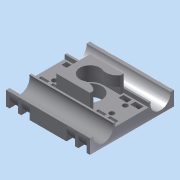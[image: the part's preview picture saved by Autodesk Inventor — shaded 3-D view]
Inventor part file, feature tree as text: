
AUTODESK INVENTOR PART (.ipt)
format: ipt  version: 2015 (Build 190159000, 159)  size: 379,392 bytes
history: native  units: in
note: dims shown in document units (in); Inventor stores cm internally (conversion verified against a paired STEP export)
features: sketch x15, extrude x10, hole x3, projected_geometry x3, move_body x3, pattern_linear x2, direct_edit x2, revolve x1
ambient origin geometry x8: Origin, YZ Plane, XZ Plane, XY Plane, X Axis, Y Axis, Z Axis, Center Point
bodies: Solid1 (feature_tree)
feature tree (39):
  sketch  "Sketch1"  dims[d0=0.7874in d1=0.7874in]
  extrude  "Extrusion1"  Depth=0.7874in
  hole  "Hole1"  [1 undecoded]
  extrude  "Extrusion2"  Depth=0.3937in
  extrude  "Extrusion3"  Depth=0.0787in
  extrude  "Extrusion4"  Depth=0.3in
  hole  "Hole2"  [1 undecoded]
  extrude  "Extrusion5"  Depth=0.1575in TaperAngle=0.0deg
  hole  "Hole3"  [1 undecoded]
  extrude  "Extrusion6"  Depth=0.5906in
  extrude  "Extrusion7"  Depth=0.4724in
  sketch  "Sketch12"  dims[d39=0.2362in d40=0.2362in]
  extrude  "Extrusion9"  Depth=0.4724in
  extrude  "Extrusion10"  Depth=0.2362in
  extrude  "Extrusion11"  Depth=0.315in TaperAngle=0.0deg
  revolve  "Revolution1"  [1 undecoded]
  pattern_linear  "Rectangular Pattern2"  Spacing1=0.2362in  [1 undecoded]
  pattern_linear  "Rectangular Pattern3"  Spacing1=0.315in  [1 undecoded]
  direct_edit  "Direct Edit1"
  direct_edit  "Direct Edit2"
  sketch  "Sketch2"  dims[d2=0.3937in d3=0.2362in d4=0.0in]
  sketch  "Sketch3"  dims[d5=0.4724in d6=0.75in d7=0.375in d8=0.25in d9=0.5635in d10=1.0in d11=0.8108in d12=0.3937in]
  sketch  "Sketch4"  dims[d13=0.0787in d14=0.0787in]
  sketch  "Sketch5"  dims[d16=0.3in d17=0.3in]
  sketch  "Sketch6"  dims[d18=0.2362in d19=0.0in d20=0.6299in]
  sketch  "Sketch7"  dims[d21=0.1575in d22=0.0in d23=0.1575in d24=0.0in]
  sketch  "Sketch8"  dims[d25=0.5512in d26=0.75in d27=0.375in d28=0.25in d29=0.5635in d30=1.0in d31=0.8108in d32=1.9685in]
  sketch  "Sketch9"  dims[d33=1.9685in d34=0.5906in]
  sketch  "Sketch10"  dims[d35=0.5906in d36=0.4724in]
  sketch  "Sketch11"  dims[d37=0.315in d38=0.4724in]
  projected_geometry  "Projected Loop1"
  projected_geometry  "Projected Loop2"
  sketch  "Sketch13"  dims[d41=0.315in d42=1.0in d43=0.0in]
  sketch  "Sketch14"  dims[d44=0.315in d45=0.315in]
  projected_geometry  "Projected Loop3"
  sketch  "Sketch15"  dims[d46=0.2362in d47=0.2362in d48=0.1181in d49=0.75in d50=0.375in d51=0.25in d52=0.5635in d53=1.0in d54=0.8108in d55=0.315in d56=0.315in d57=0.0787in d58=1.0in d59=0.0in d60=0.1969in d61=0.0in d62=0.6693in d63=0.0787in d66=0.0394in d67=0.0in d68=0.0394in d69=0.0in d70=0.0394in d71=0.0in d79=0.2756in d80=0.0787in d81=0.1969in d82=90.0deg d83=0.7874in d85=0.2756in d86=0.7874in d88=1.3386in d89=0.1181in d90=0.0394in d91=0.7874in d93=1.3386in d94=0.2756in d95=0.0in d96=0.0in d97=0.1969in d98=0.0in d99=0.0in d100=-0.1969in d101=0.0in d102=0.0in d103=0.1969in]
  move_body  "Move1"
  move_body  "Move2"
  move_body  "Move3"
note: 6 required parameter values undecoded (feature->parameter linkage not recoverable at this tier; creation-order binding heuristic only, values carry confidence <= 0.55)